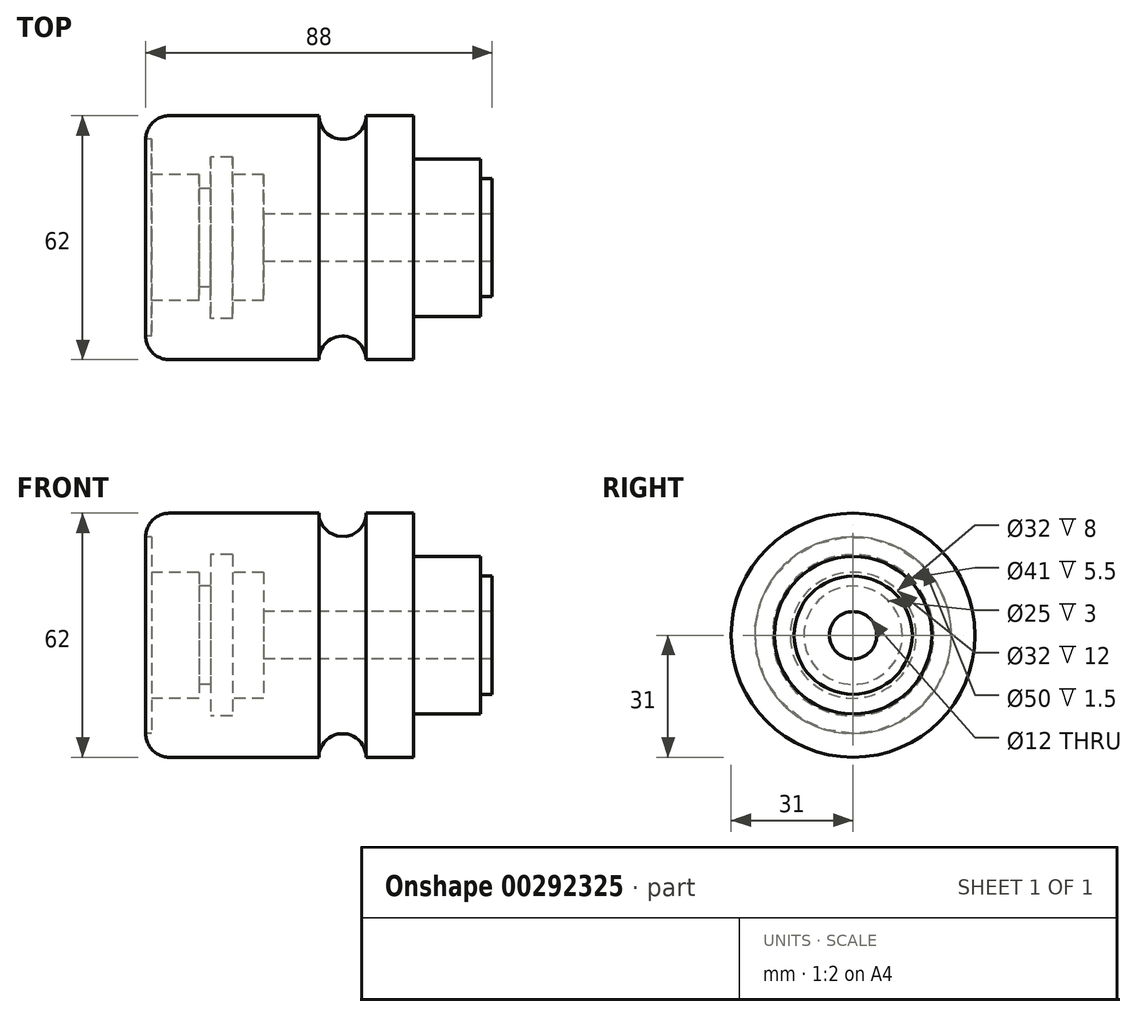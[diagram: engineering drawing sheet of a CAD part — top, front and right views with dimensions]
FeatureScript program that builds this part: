
annotation { "Feature Type Name" : "Feature", "Feature Type Description" : "" }
export const myFeature = defineFeature(function(context is Context, id is Id, definition is map)
    precondition{}
    {
        {
            var Q0;
            Q0=qCreatedBy(makeId("Front.planeOp"),FACE);
            var sketch = newSketch(context, id + "F0", { "sketchPlane" : qUnion([Q0])});
            skLineSegment(sketch, "E0", {"start": v(0, 0) * mm, "end": v(77.68, 0) * mm, "construction": true});
            skLineSegment(sketch, "E1", {"start": v(0, 0) * mm, "end": v(0, 31) * mm});
            skLineSegment(sketch, "E2", {"start": v(0, 31) * mm, "end": v(44, 31) * mm});
            skLineSegment(sketch, "E3", {"start": v(68, 31) * mm, "end": v(68, 20) * mm});
            skLineSegment(sketch, "E4", {"start": v(68, 20) * mm, "end": v(85, 20) * mm});
            skLineSegment(sketch, "E5", {"start": v(85, 20) * mm, "end": v(85, 15) * mm});
            skLineSegment(sketch, "E6", {"start": v(85, 15) * mm, "end": v(88, 15) * mm});
            skLineSegment(sketch, "E7", {"start": v(88, 15) * mm, "end": v(88, 0) * mm});
            skLineSegment(sketch, "E8", {"start": v(88, 0) * mm, "end": v(0, 0) * mm});
            skArc(sketch, "E9", {"start": v(44, 31) * mm, "mid": v(50, 25) * mm, "end": v(56, 31) * mm});
            skLineSegment(sketch, "E10.trimOffspring", {"start": v(56, 31) * mm, "end": v(68, 31) * mm});
            skSolve(sketch);
        }
        {
            var Q0;
            Q0 = qSketchRegion(id + "F0", true);
            var Q1;
            Q1=sQuery(id+"F0.wireOp",EDGE,"E8");
            revolve(context, id + "F1", {"entities" : qUnion([Q0]), "axis" : qUnion([Q1]), "revolveType" : RevolveType.FULL});
        }
        {
            var Q0;
            Q0=qCreatedBy(makeId("Front.planeOp"),FACE);
            var sketch = newSketch(context, id + "F2", { "sketchPlane" : qUnion([Q0])});
            skLineSegment(sketch, "E11", {"start": v(0, 0) * mm, "end": v(0, 25) * mm});
            skLineSegment(sketch, "E12", {"start": v(0, 25) * mm, "end": v(1.5, 25) * mm});
            skLineSegment(sketch, "E13", {"start": v(1.5, 25) * mm, "end": v(1.5, 16) * mm});
            skLineSegment(sketch, "E14", {"start": v(1.5, 16) * mm, "end": v(13.5, 16) * mm});
            skLineSegment(sketch, "E15", {"start": v(13.5, 16) * mm, "end": v(13.5, 12.5) * mm});
            skLineSegment(sketch, "E16", {"start": v(13.5, 12.5) * mm, "end": v(16.5, 12.5) * mm});
            skLineSegment(sketch, "E17", {"start": v(22, 16) * mm, "end": v(30, 16) * mm});
            skLineSegment(sketch, "E18", {"start": v(30, 16) * mm, "end": v(30, 6) * mm});
            skLineSegment(sketch, "E19", {"start": v(30, 6) * mm, "end": v(88, 6) * mm});
            skLineSegment(sketch, "E20", {"start": v(88, 6) * mm, "end": v(88, 0) * mm});
            skLineSegment(sketch, "E21", {"start": v(88, 0) * mm, "end": v(0, 0) * mm});
            skLineSegment(sketch, "E22", {"start": v(0, 0) * mm, "end": v(-20.42, 0) * mm, "construction": true});
            skLineSegment(sketch, "E23", {"start": v(16.5, 12.5) * mm, "end": v(16.5, 20.5) * mm});
            skLineSegment(sketch, "E24", {"start": v(16.5, 20.5) * mm, "end": v(22, 20.5) * mm});
            skLineSegment(sketch, "E25", {"start": v(22, 20.5) * mm, "end": v(22, 16) * mm});
            skSolve(sketch);
        }
        {
            var Q0;
            Q0 = qSketchRegion(id + "F2", true);
            var Q1;
            Q1=sQuery(id+"F2.wireOp",EDGE,"E22");
            revolve(context, id + "F3", {"operationType" : NewBodyOperationType.REMOVE, "entities" : qUnion([Q0]), "axis" : qUnion([Q1]), "revolveType" : RevolveType.FULL, "oppositeDirection" : true});
        }
        {
            var Q0;
            Q0=makeQuery(id+"F1.opRevolve","SWEPT_EDGE",EDGE,{"disambiguationData":[OSD([sQuery(id+"F0.wireOp",EDGE,"E1"),sQuery(id+"F0.wireOp",EDGE,"E2")])]});
            fillet(context, id + "F4", {"entities" : qUnion([Q0]), "radius" : 6 * mm, "tangentPropagation" : true, "allowEdgeOverflow" : false});
        }
    });
